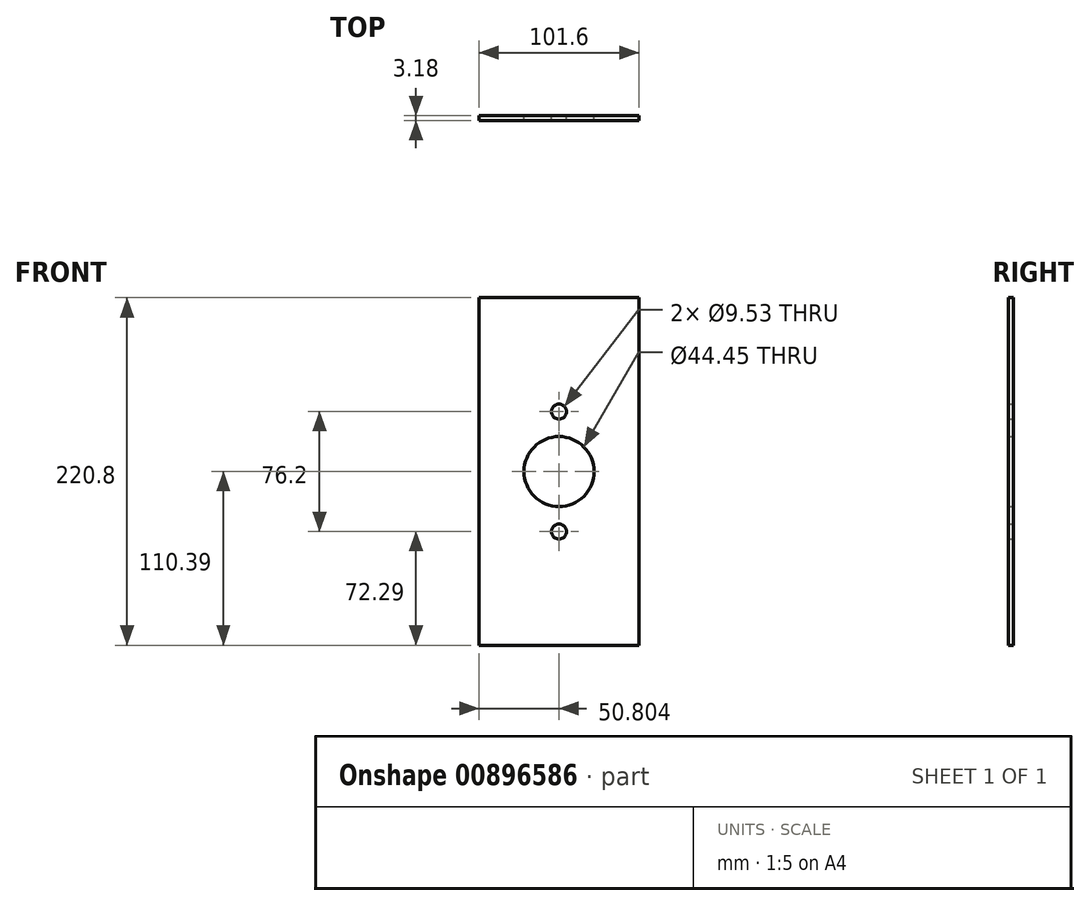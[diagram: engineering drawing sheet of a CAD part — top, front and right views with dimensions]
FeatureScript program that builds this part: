
annotation { "Feature Type Name" : "Feature", "Feature Type Description" : "" }
export const myFeature = defineFeature(function(context is Context, id is Id, definition is map)
    precondition{}
    {
        {
            var Q0;
            Q0=qCreatedBy(makeId("Front.planeOp"),FACE);
            var sketch = newSketch(context, id + "F0", { "sketchPlane" : qUnion([Q0])});
            skCircle(sketch, "E0", {"center": v(296.71, 38.1) * mm, "radius": 22.23 * mm});
            skCircle(sketch, "E1", {"center": v(296.71, 76.2) * mm, "radius": 4.76 * mm});
            skCircle(sketch, "E2", {"center": v(296.71, 0) * mm, "radius": 4.76 * mm});
            skLineSegment(sketch, "E3", {"start": v(347.51, 38.1) * mm, "end": v(347.51, 148.51) * mm});
            skLineSegment(sketch, "E4", {"start": v(347.51, 38.1) * mm, "end": v(347.51, -72.29) * mm});
            skLineSegment(sketch, "E5", {"start": v(245.91, -72.29) * mm, "end": v(347.51, -72.29) * mm});
            skLineSegment(sketch, "E6", {"start": v(245.91, 148.51) * mm, "end": v(347.51, 148.51) * mm});
            skLineSegment(sketch, "E7", {"start": v(245.91, 148.51) * mm, "end": v(245.91, -72.29) * mm});
            skSolve(sketch);
        }
        {
            var Q0;
            Q0=makeQuery(id+"F0.imprint","IMPRINT",FACE,{"disambiguationData":[TD([[makeQuery(id+"F0.imprint","IMPRINT",EDGE,{"derivedFrom":sQuery(id+"F0.wireOp",EDGE,"E0")}),-1.0]])]});
            extrude(context, id + "F1", {"entities" : qUnion([Q0]), "depth" : 3.17 * mm, "offsetDistance" : 25.4 * mm});
        }
    });
